# Revit family: Hitachi_Silent-iconic-design-white-EU_LOD400
name_source: partatom
category: Mechanical Equipment
revit_build: Autodesk Revit 2018 (Build: 20170223_1515(x64)
units: mm (PartAtom-declared; Revit-internal decimal feet)

## family parameters
Always vertical = Yes
Classification = None
Cut with Voids When Loaded = No
OmniClass Number = 23.75.70.00
OmniClass Title = HVAC Distribution Devices
Part Type = Normal
Room Calculation Point = No
Round Connector Dimension = Use Diameter
Shared = No
Work Plane-Based = No

## types (8) — shared parameters
BC_MODEL_ID = 1194584
BC_OBJECT_ID = 428635
BC_OBJECT_VERSION = #3
Connection type = flare-nut connection
Frequency = 50 Hz
Indoor fan - Air Flow Rate (Hi) = 1380.0 m³/h
Indoor fan - Air Flow Rate (Hi2) = 1620.0 m³/h
Indoor fan - Air Flow Rate (Lo) = 900.0 m³/h
Indoor fan - Air Flow Rate (Me) = 1080.0 m³/h
Manufacturer = Hitachi Air Conditioning Europe SAS
MasterFormat = Indoor Central-Station Air-Handling Units
Masterformat Code = 23 73 00
Maximum AC Voltage = 253 V
Minimum AC Voltage = 207 V
Model = 4-way cassette Design Panel Silent-Iconic (Standard White) - EU
Name BIM&CO = Indoor Unit
Nominal Voltage = 230 V
Number of Phases = 1
OmniClass code = 23-33 25 00
OmniClass description = Air Handling Units
Outlet Diameter = 32 mm
Overall depth = 950 mm
Overall height = 328 mm
Overall width = 950 mm
RCI Height = 298 mm
Reference description = Standard (Natural White)
Uniformat = Distribution Systems
Uniformat code = D3040

## per-type parameters (varying)
| type | BC_VARIANT_ID | Gas Diameter | Liquid Diameter | Net Weight | Nominal Cooling Capacity | Nominal Heating Capacity | Product Code | Sound Pressure Level (Hi2) | Sound Pressure Level (Lo) | Sound Pressure Level (Me) | Sound Pressure Level (hi) |
| RCI-1.0FSR1 + P-GP160NAP | 963914 | 13 mm  [stored 0.0426509 ft] | 6 mm  [stored 0.019685 ft] | 28.50 kg | 2800 W | 3200 W | RCI-1.0FSRP + P-GP160NAP | 35 | 29 | 30 | 32 |
| RCI-1.5FSR1 + P-GP160NAP | 963915 | 13 mm  [stored 0.0426509 ft] | 6 mm  [stored 0.019685 ft] | 29.50 kg | 4000 W | 4800 W | RCI-1.5FSRP + P-GP160NAP | 37 | 29 | 32 | 33 |
| RCI-2.0FSR1 + P-GP160NAP | 963916 | 13 mm  [stored 0.0426509 ft] | 6 mm  [stored 0.019685 ft] | 29.50 kg | 5600 W | 6300 W | RCI-2.0FSRP + P-GP160NAP | 39 | 30 | 32 | 34 |
| RCI-2.5FSR1 + P-GP160NAP | 963917 | 16 mm  [stored 0.0524934 ft] | 10 mm  [stored 0.0328084 ft] | 30.50 kg | 7100 W | 8500 W | RCI-2.5FSRP + P-GP160NAP | 45 | 31 | 35 | 39 |
| RCI-3.0FSR1 + P-GP160NAP | 963918 | 16 mm  [stored 0.0524934 ft] | 10 mm  [stored 0.0328084 ft] | 34.50 kg | 8000 W | 9000 W | RCI-3.0FSRP + P-GP160NAP | 43 | 32 | 34 | 38 |
| RCI-4.0FSR1 + P-GP160NAP | 963919 | 16 mm  [stored 0.0524934 ft] | 10 mm  [stored 0.0328084 ft] | 34.50 kg | 11200 W | 12500 W | RCI-4.0FSRP + P-GP160NAP | 51 | 35 | 41 | 46 |
| RCI-5.0FSR1 + P-GP160NAP | 963920 | 16 mm  [stored 0.0524934 ft] | 10 mm  [stored 0.0328084 ft] | 34.50 kg | 14000 W | 16000 W | RCI-5.0FSRP + P-GP160NAP | 51 | 37 | 43 | 48 |
| RCI-6.0FSR1 + P-GP160NAP | 963921 | 16 mm  [stored 0.0524934 ft] | 10 mm  [stored 0.0328084 ft] | 34.50 kg | 16000 W | 18000 W | RCI-6.0FSRP + P-GP160NAP | 51 | 49 | 45 | 49 |

note: column(s) folded — value = type name in every type: Reference

note: [stored X ft] marks values corroborated as IEEE doubles in the binary element streams (Revit-internal decimal feet)
